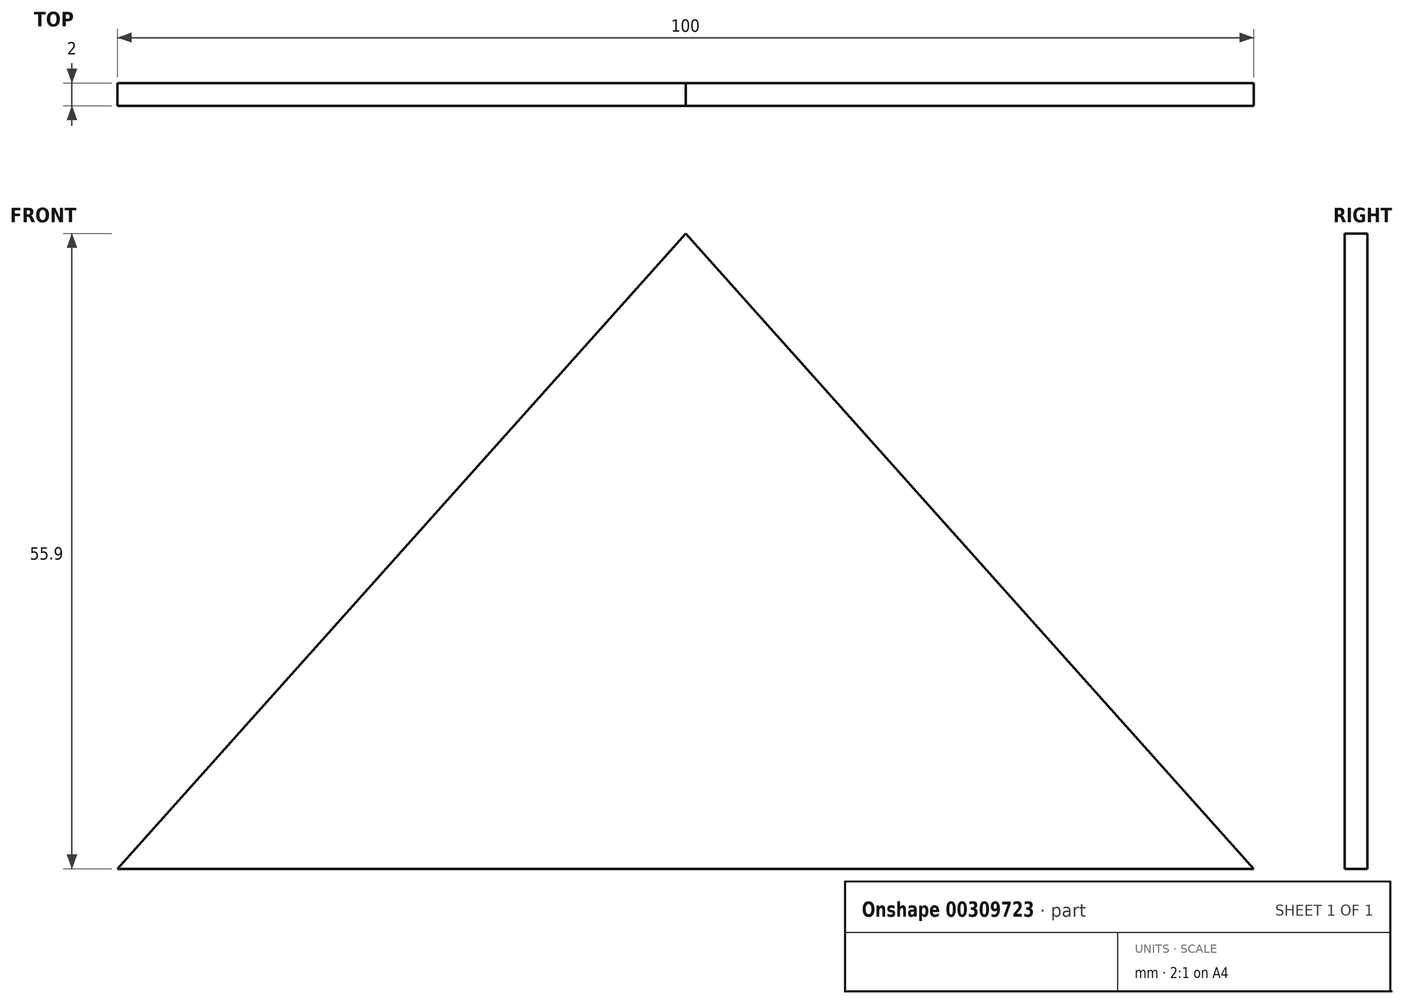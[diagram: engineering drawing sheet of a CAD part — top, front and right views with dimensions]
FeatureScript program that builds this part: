
annotation { "Feature Type Name" : "Feature", "Feature Type Description" : "" }
export const myFeature = defineFeature(function(context is Context, id is Id, definition is map)
    precondition{}
    {
        {
            var Q0;
            Q0=qCreatedBy(makeId("Front.planeOp"),FACE);
            var sketch = newSketch(context, id + "F0", { "sketchPlane" : qUnion([Q0])});
            skLineSegment(sketch, "E0", {"start": v(0, 0) * mm, "end": v(50, 55.9) * mm});
            skLineSegment(sketch, "E1", {"start": v(50, 55.9) * mm, "end": v(100, 0) * mm});
            skLineSegment(sketch, "E2", {"start": v(100, 0) * mm, "end": v(0, 0) * mm});
            skSolve(sketch);
        }
        {
            var Q0;
            Q0=makeQuery(id+"F0.imprint","IMPRINT",FACE,{"disambiguationData":[TD([[makeQuery(id+"F0.imprint","IMPRINT",EDGE,{"derivedFrom":sQuery(id+"F0.wireOp",EDGE,"E0")}),-1.0]])]});
            extrude(context, id + "F1", {"entities" : qUnion([Q0]), "depth" : 2 * mm});
        }
    });
